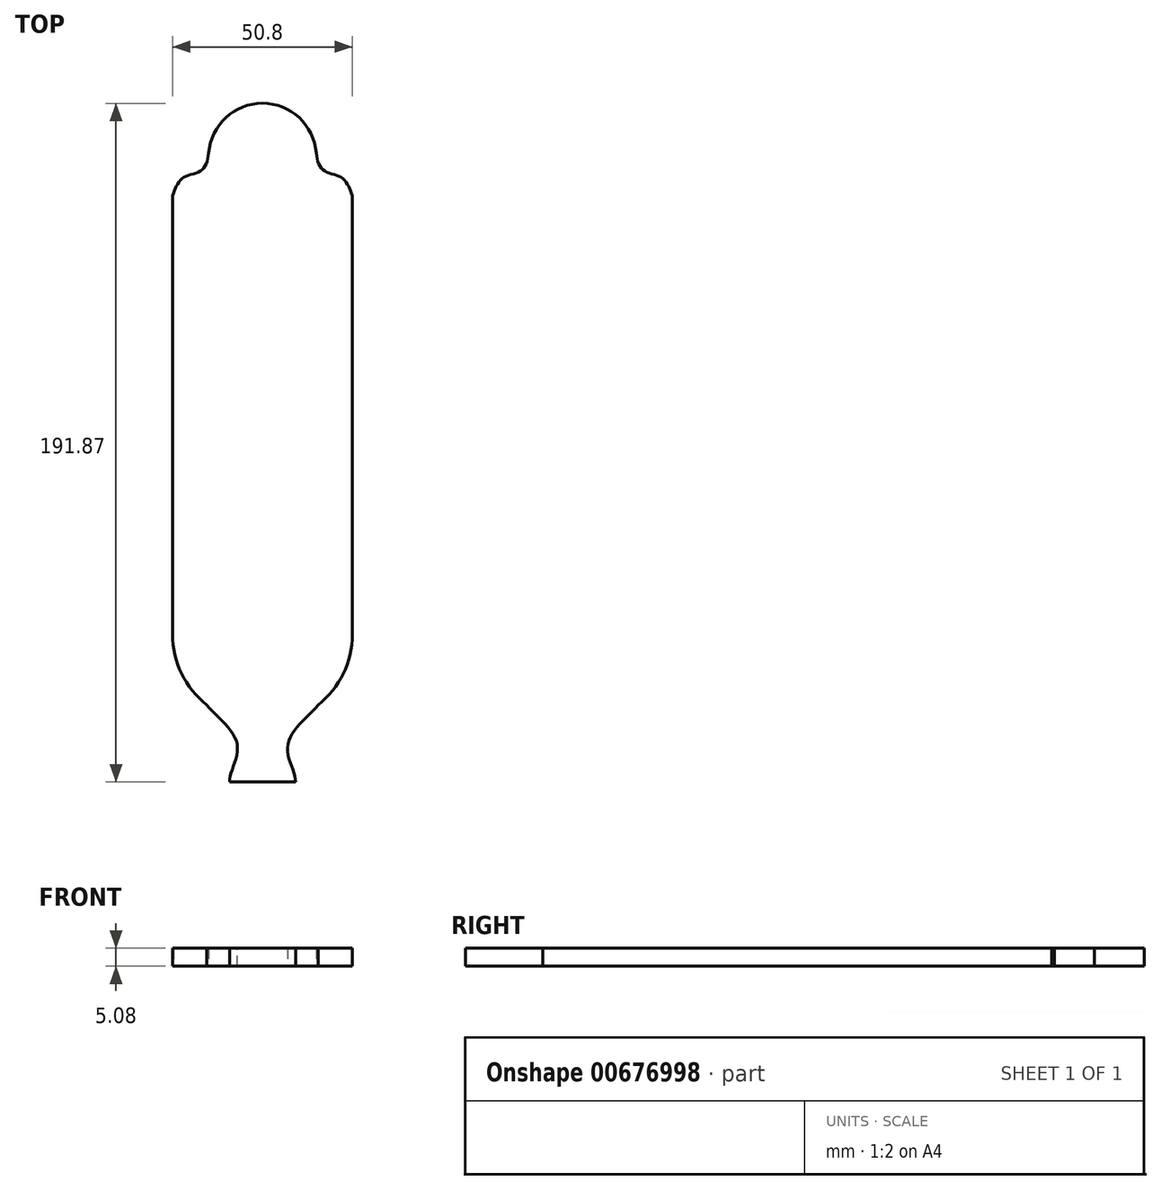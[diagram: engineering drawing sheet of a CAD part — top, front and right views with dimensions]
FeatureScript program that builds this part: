
annotation { "Feature Type Name" : "Feature", "Feature Type Description" : "" }
export const myFeature = defineFeature(function(context is Context, id is Id, definition is map)
    precondition{}
    {
        {
            var Q0;
            Q0=qCreatedBy(makeId("Top.planeOp"),FACE);
            var sketch = newSketch(context, id + "F0", { "sketchPlane" : qUnion([Q0])});
            skArc(sketch, "E0", {"start": v(-25.4, 124.07) * mm, "mid": v(0, 98.67) * mm, "end": v(25.4, 124.07) * mm});
            skCircle(sketch, "E1", {"center": v(0, 0) * mm, "radius": 25.4 * mm});
            skLineSegment(sketch, "E2", {"start": v(-25.4, 124.07) * mm, "end": v(-25.4, 0) * mm});
            skLineSegment(sketch, "E3.MirrorCS", {"start": v(25.4, 124.07) * mm, "end": v(25.4, 0) * mm});
            skCircle(sketch, "E4", {"center": v(0, 134.93) * mm, "radius": 15.24 * mm});
            skLineSegment(sketch, "E5", {"start": v(-25.4, 124.07) * mm, "end": v(-25.4, 124.07) * mm});
            skLineSegment(sketch, "E6.MirrorCS", {"start": v(25.4, 124.07) * mm, "end": v(25.4, 124.07) * mm});
            skPoint(sketch, "E7", {"position": v(-1.68, -8.62) * mm});
            skPoint(sketch, "E8.MirrorP", {"position": v(1.68, -8.62) * mm});
            skLineSegment(sketch, "E9.trimOffspring", {"start": v(-1.2, 119.74) * mm, "end": v(-1.2, 119.74) * mm});
            skLineSegment(sketch, "E10.trimOffspring", {"start": v(1.2, 119.74) * mm, "end": v(1.2, 119.74) * mm});
            skPoint(sketch, "E11.MirrorCS.end.orphan", {"position": v(15.8, -19.9) * mm});
            skPoint(sketch, "E12.1.internal.orphan", {"position": v(-1.68, -6.88) * mm});
            skPoint(sketch, "E12.end.orphan", {"position": v(-15.8, -19.9) * mm});
            skFitSpline(sketch, "E13", {"points": [v(-25.2, 124.75) * mm, v(-22.34, 129.16) * mm, v(-17.04, 131.38) * mm, v(-15.02, 137.51) * mm], "startDerivative": vector(6.54, 16.47) * mm, "endDerivative": vector(2.44, 20.9) * mm});
            skLineSegment(sketch, "E14", {"start": v(0, -25.4) * mm, "end": v(0, 183.84) * mm});
            skLineSegment(sketch, "E15", {"start": v(0, 183.84) * mm, "end": v(0, -55.08) * mm});
            skFitSpline(sketch, "E16.MirrorCS", {"points": [v(25.2, 124.75) * mm, v(22.34, 129.16) * mm, v(17.04, 131.38) * mm, v(15.02, 137.51) * mm], "startDerivative": vector(-6.54, 16.47) * mm, "endDerivative": vector(-2.44, 20.9) * mm});
            skPoint(sketch, "E17", {"position": v(-9.34, -41.7) * mm});
            skPoint(sketch, "E18.MirrorP", {"position": v(9.34, -41.7) * mm});
            skLineSegment(sketch, "E19", {"start": v(-9.34, -41.7) * mm, "end": v(9.34, -41.7) * mm});
            skFitSpline(sketch, "E20", {"points": [v(-9.34, -41.7) * mm, v(-7.11, -31.45) * mm, v(-15.8, -19.9) * mm], "startDerivative": vector(-0.72, 17.25) * mm, "endDerivative": vector(-18.37, 20.54) * mm});
            skFitSpline(sketch, "E21.MirrorCS", {"points": [v(9.34, -41.7) * mm, v(7.11, -31.45) * mm, v(15.8, -19.9) * mm], "startDerivative": vector(0.72, 17.25) * mm, "endDerivative": vector(18.37, 20.54) * mm});
            skLineSegment(sketch, "E22", {"start": v(25.2, 124.75) * mm, "end": v(25.4, 124.07) * mm});
            skLineSegment(sketch, "E23.MirrorCS", {"start": v(-25.2, 124.75) * mm, "end": v(-25.4, 124.07) * mm});
            skSolve(sketch);
        }
        {
            var Q0;
            Q0 = qSketchRegion(id + "F0", true);
            extrude(context, id + "F1", {"entities" : qUnion([Q0]), "endBound" : BoundingType.SYMMETRIC, "depth" : 5.08 * mm, "offsetDistance" : 25.4 * mm});
        }
    });
